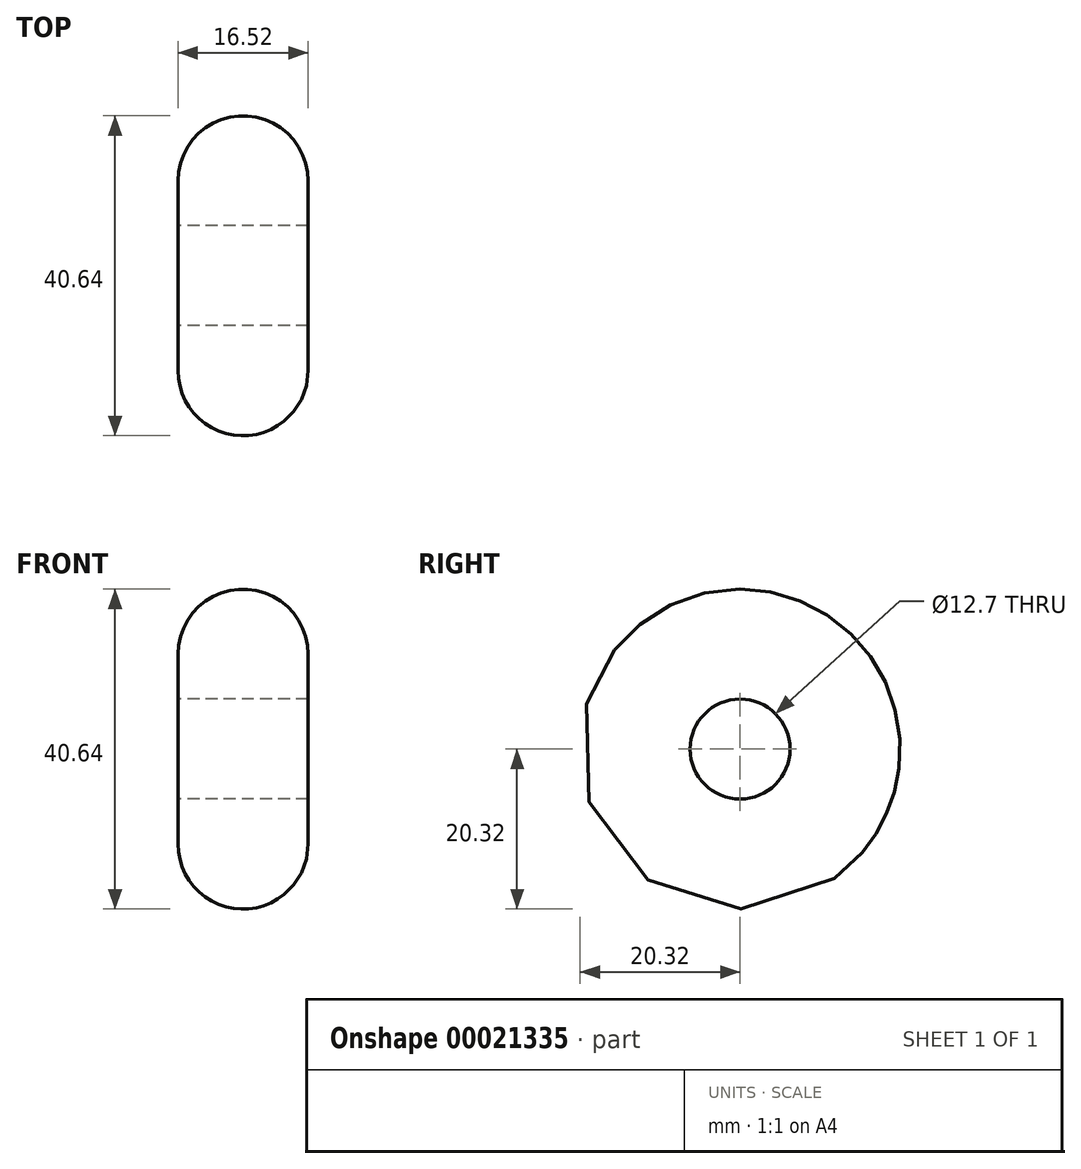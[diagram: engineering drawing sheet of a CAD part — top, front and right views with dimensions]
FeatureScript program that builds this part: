
annotation { "Feature Type Name" : "Feature", "Feature Type Description" : "" }
export const myFeature = defineFeature(function(context is Context, id is Id, definition is map)
    precondition{}
    {
        {
            var Q0;
            Q0=qCreatedBy(makeId("Front.planeOp"),FACE);
            var sketch = newSketch(context, id + "F0", { "sketchPlane" : qUnion([Q0])});
            skLineSegment(sketch, "E0", {"start": v(0, 0) * mm, "end": v(18.97, 0) * mm, "construction": true});
            skLineSegment(sketch, "E1", {"start": v(0, 6.35) * mm, "end": v(8.26, 6.35) * mm});
            skLineSegment(sketch, "E2", {"start": v(8.26, 6.35) * mm, "end": v(8.26, 12.07) * mm});
            skArc(sketch, "E3", {"start": v(8.26, 12.07) * mm, "mid": v(5.84, 17.9) * mm, "end": v(0, 20.32) * mm});
            skLineSegment(sketch, "E4", {"start": v(0, 0) * mm, "end": v(0, 6.62) * mm, "construction": true});
            skLineSegment(sketch, "E5.MirrorCS", {"start": v(0, 6.35) * mm, "end": v(-8.26, 6.35) * mm});
            skLineSegment(sketch, "E6.MirrorCS", {"start": v(-8.26, 6.35) * mm, "end": v(-8.26, 12.07) * mm});
            skArc(sketch, "E7.MirrorCS", {"start": v(-8.26, 12.07) * mm, "mid": v(-5.84, 17.9) * mm, "end": v(0, 20.32) * mm});
            skSolve(sketch);
        }
        {
            var Q0;
            Q0 = qSketchRegion(id + "F0", true);
            var Q1;
            Q1=sQuery(id+"F0.wireOp",EDGE,"E0");
            revolve(context, id + "F1", {"entities" : qUnion([Q0]), "axis" : qUnion([Q1]), "revolveType" : RevolveType.FULL});
        }
    });
